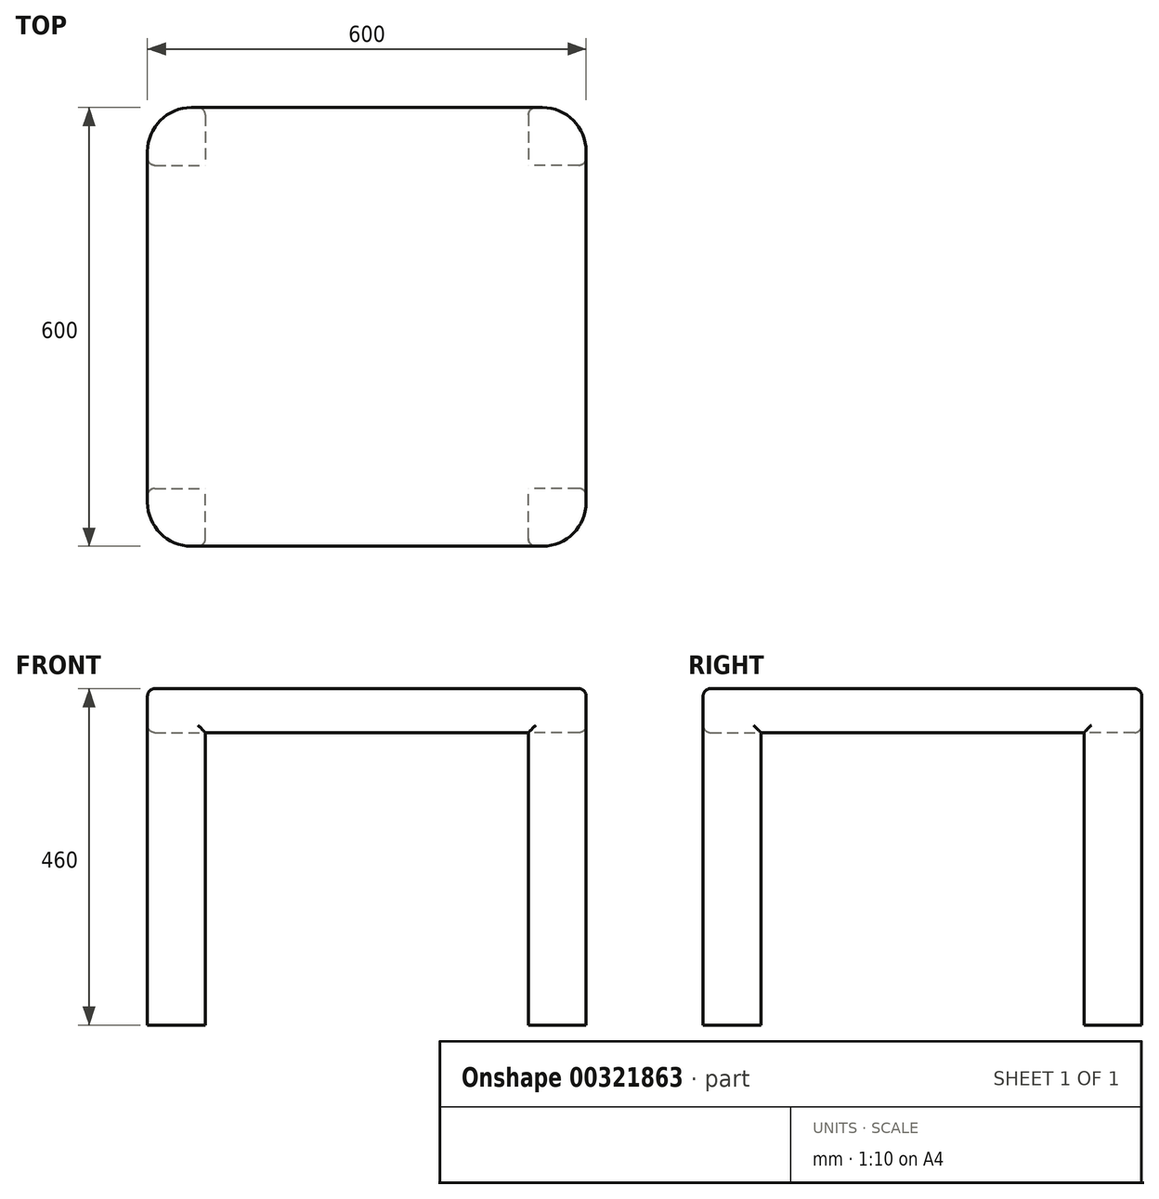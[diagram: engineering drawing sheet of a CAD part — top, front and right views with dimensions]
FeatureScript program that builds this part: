
annotation { "Feature Type Name" : "Feature", "Feature Type Description" : "" }
export const myFeature = defineFeature(function(context is Context, id is Id, definition is map)
    precondition{}
    {
        {
            var Q0;
            Q0=qCreatedBy(makeId("Top.planeOp"),FACE);
            var sketch = newSketch(context, id + "F0", { "sketchPlane" : qUnion([Q0])});
            skLineSegment(sketch, "E0.bottom", {"start": v(300, 300) * mm, "end": v(-300, 300) * mm});
            skLineSegment(sketch, "E0.top", {"start": v(300, -300) * mm, "end": v(-300, -300) * mm});
            skLineSegment(sketch, "E0.left", {"start": v(300, 300) * mm, "end": v(300, -300) * mm});
            skLineSegment(sketch, "E0.right", {"start": v(-300, 300) * mm, "end": v(-300, -300) * mm});
            skPoint(sketch, "E0.middle", {"position": v(0, 0) * mm});
            skSolve(sketch);
        }
        {
            var Q0;
            Q0=makeQuery(id+"F0.imprint","IMPRINT",FACE,{"disambiguationData":[TD([[makeQuery(id+"F0.imprint","IMPRINT",EDGE,{"derivedFrom":sQuery(id+"F0.wireOp",EDGE,"E0.bottom")}),1.0]])]});
            extrude(context, id + "F1", {"entities" : qUnion([Q0]), "depth" : 60 * mm});
        }
        {
            var Q0;
            Q0=makeQuery(id+"F1.opExtrude","CAP_FACE",FACE,{"disambiguationData":[OSD([sQuery(id+"F0.wireOp",EDGE,"E0.bottom"),sQuery(id+"F0.wireOp",EDGE,"E0.top"),sQuery(id+"F0.wireOp",EDGE,"E0.left"),sQuery(id+"F0.wireOp",EDGE,"E0.right")])],"isStart":true});
            var sketch = newSketch(context, id + "F2", { "sketchPlane" : qUnion([Q0])});
            skLineSegment(sketch, "E1", {"start": v(-300, 0) * mm, "end": v(300, 0) * mm});
            skLineSegment(sketch, "E2", {"start": v(0, -300) * mm, "end": v(0, 300) * mm});
            skLineSegment(sketch, "E3.bottom", {"start": v(-300, 300) * mm, "end": v(-220.95, 300) * mm});
            skLineSegment(sketch, "E3.top", {"start": v(-300, 220.95) * mm, "end": v(-220.95, 220.95) * mm});
            skLineSegment(sketch, "E3.left", {"start": v(-300, 300) * mm, "end": v(-300, 220.95) * mm});
            skLineSegment(sketch, "E3.right", {"start": v(-220.95, 300) * mm, "end": v(-220.95, 220.95) * mm});
            skLineSegment(sketch, "E4.MirrorCS", {"start": v(300, 220.95) * mm, "end": v(220.95, 220.95) * mm});
            skLineSegment(sketch, "E5.MirrorCS", {"start": v(300, 300) * mm, "end": v(300, 220.95) * mm});
            skLineSegment(sketch, "E6.MirrorCS", {"start": v(220.95, 300) * mm, "end": v(220.95, 220.95) * mm});
            skLineSegment(sketch, "E7.MirrorCS", {"start": v(300, 300) * mm, "end": v(220.95, 300) * mm});
            skLineSegment(sketch, "E8.MirrorCS", {"start": v(300, 0) * mm, "end": v(-300, 0) * mm});
            skLineSegment(sketch, "E9.MirrorCS", {"start": v(-220.95, -300) * mm, "end": v(-220.95, -220.95) * mm});
            skLineSegment(sketch, "E10.MirrorCS", {"start": v(-300, -300) * mm, "end": v(-220.95, -300) * mm});
            skLineSegment(sketch, "E11.MirrorCS", {"start": v(-300, -300) * mm, "end": v(-300, -220.95) * mm});
            skLineSegment(sketch, "E12.MirrorCS", {"start": v(-300, -220.95) * mm, "end": v(-220.95, -220.95) * mm});
            skLineSegment(sketch, "E13.MirrorCS", {"start": v(300, -300) * mm, "end": v(220.95, -300) * mm});
            skLineSegment(sketch, "E14.MirrorCS", {"start": v(220.95, -300) * mm, "end": v(220.95, -220.95) * mm});
            skLineSegment(sketch, "E15.MirrorCS", {"start": v(300, -220.95) * mm, "end": v(220.95, -220.95) * mm});
            skLineSegment(sketch, "E16.MirrorCS", {"start": v(300, -300) * mm, "end": v(300, -220.95) * mm});
            skSolve(sketch);
        }
        {
            var Q0;
            Q0 = qSketchRegion(id + "F2", true);
            extrude(context, id + "F3", {"entities" : qUnion([Q0]), "operationType" : NewBodyOperationType.ADD, "depth" : 400 * mm});
        }
        {
            var Q0;
            Q0=makeQuery(id+"F3.boolean.opBoolean","MERGE",EDGE,{"derivedFrom":[makeQuery(id+"F1.opExtrude","SWEPT_EDGE",EDGE,{"disambiguationData":[OSD([sQuery(id+"F0.wireOp",EDGE,"E0.top"),sQuery(id+"F0.wireOp",EDGE,"E0.right")])]}),makeQuery(id+"F3.opExtrude","SWEPT_EDGE",EDGE,{"disambiguationData":[OSD([sQuery(id+"F2.wireOp",EDGE,"E3.bottom"),sQuery(id+"F2.wireOp",EDGE,"E3.left")])]})]});
            var Q1;
            Q1=makeQuery(id+"F3.boolean.opBoolean","MERGE",EDGE,{"derivedFrom":[makeQuery(id+"F1.opExtrude","SWEPT_EDGE",EDGE,{"disambiguationData":[OSD([sQuery(id+"F0.wireOp",EDGE,"E0.bottom"),sQuery(id+"F0.wireOp",EDGE,"E0.right")])]}),makeQuery(id+"F3.opExtrude","SWEPT_EDGE",EDGE,{"disambiguationData":[OSD([sQuery(id+"F2.wireOp",EDGE,"E10.MirrorCS"),sQuery(id+"F2.wireOp",EDGE,"E11.MirrorCS")])]})]});
            var Q2;
            Q2=makeQuery(id+"F3.boolean.opBoolean","MERGE",EDGE,{"derivedFrom":[makeQuery(id+"F1.opExtrude","SWEPT_EDGE",EDGE,{"disambiguationData":[OSD([sQuery(id+"F0.wireOp",EDGE,"E0.bottom"),sQuery(id+"F0.wireOp",EDGE,"E0.left")])]}),makeQuery(id+"F3.opExtrude","SWEPT_EDGE",EDGE,{"disambiguationData":[OSD([sQuery(id+"F2.wireOp",EDGE,"E13.MirrorCS"),sQuery(id+"F2.wireOp",EDGE,"E16.MirrorCS")])]})]});
            var Q3;
            Q3=makeQuery(id+"F3.boolean.opBoolean","MERGE",EDGE,{"derivedFrom":[makeQuery(id+"F1.opExtrude","SWEPT_EDGE",EDGE,{"disambiguationData":[OSD([sQuery(id+"F0.wireOp",EDGE,"E0.top"),sQuery(id+"F0.wireOp",EDGE,"E0.left")])]}),makeQuery(id+"F3.opExtrude","SWEPT_EDGE",EDGE,{"disambiguationData":[OSD([sQuery(id+"F2.wireOp",EDGE,"E5.MirrorCS"),sQuery(id+"F2.wireOp",EDGE,"E7.MirrorCS")])]})]});
            fillet(context, id + "F4", {"entities" : qUnion([Q0, Q1, Q2, Q3]), "radius" : 60 * mm, "tangentPropagation" : true, "allowEdgeOverflow" : false});
        }
        {
            var Q0;
            Q0=makeQuery(id+"F1.opExtrude","CAP_EDGE",EDGE,{"disambiguationData":[OSD([sQuery(id+"F0.wireOp",EDGE,"E0.bottom")])],"isStart":false});
            var Q1;
            Q1=makeQuery(id+"F1.opExtrude","CAP_EDGE",EDGE,{"disambiguationData":[OSD([sQuery(id+"F0.wireOp",EDGE,"E0.bottom")])],"isStart":true});
            var Q2;
            Q2=makeQuery(id+"F3.opExtrude","SWEPT_EDGE",EDGE,{"disambiguationData":[OSD([sQuery(id+"F0.wireOp",EDGE,"E0.bottom"),sQuery(id+"F2.wireOp",EDGE,"E13.MirrorCS"),sQuery(id+"F2.wireOp",EDGE,"E14.MirrorCS")])]});
            var Q3;
            Q3=makeQuery(id+"F3.opExtrude","SWEPT_EDGE",EDGE,{"disambiguationData":[OSD([sQuery(id+"F0.wireOp",EDGE,"E0.bottom"),sQuery(id+"F2.wireOp",EDGE,"E9.MirrorCS"),sQuery(id+"F2.wireOp",EDGE,"E10.MirrorCS")])]});
            var Q4;
            Q4=makeQuery(id+"F1.opExtrude","CAP_EDGE",EDGE,{"disambiguationData":[OSD([sQuery(id+"F0.wireOp",EDGE,"E0.right")])],"isStart":true});
            var Q5;
            Q5=makeQuery(id+"F3.opExtrude","SWEPT_EDGE",EDGE,{"disambiguationData":[OSD([sQuery(id+"F0.wireOp",EDGE,"E0.right"),sQuery(id+"F2.wireOp",EDGE,"E11.MirrorCS"),sQuery(id+"F2.wireOp",EDGE,"E12.MirrorCS")])]});
            var Q6;
            Q6=makeQuery(id+"F3.opExtrude","SWEPT_EDGE",EDGE,{"disambiguationData":[OSD([sQuery(id+"F0.wireOp",EDGE,"E0.right"),sQuery(id+"F2.wireOp",EDGE,"E3.top"),sQuery(id+"F2.wireOp",EDGE,"E3.left")])]});
            var Q7;
            Q7=makeQuery(id+"F1.opExtrude","CAP_EDGE",EDGE,{"disambiguationData":[OSD([sQuery(id+"F0.wireOp",EDGE,"E0.top")])],"isStart":true});
            var Q8;
            Q8=makeQuery(id+"F3.opExtrude","SWEPT_EDGE",EDGE,{"disambiguationData":[OSD([sQuery(id+"F0.wireOp",EDGE,"E0.top"),sQuery(id+"F2.wireOp",EDGE,"E3.bottom"),sQuery(id+"F2.wireOp",EDGE,"E3.right")])]});
            var Q9;
            Q9=makeQuery(id+"F3.opExtrude","SWEPT_EDGE",EDGE,{"disambiguationData":[OSD([sQuery(id+"F0.wireOp",EDGE,"E0.top"),sQuery(id+"F2.wireOp",EDGE,"E6.MirrorCS"),sQuery(id+"F2.wireOp",EDGE,"E7.MirrorCS")])]});
            var Q10;
            Q10=makeQuery(id+"F1.opExtrude","CAP_EDGE",EDGE,{"disambiguationData":[OSD([sQuery(id+"F0.wireOp",EDGE,"E0.left")])],"isStart":true});
            var Q11;
            Q11=makeQuery(id+"F3.opExtrude","SWEPT_EDGE",EDGE,{"disambiguationData":[OSD([sQuery(id+"F0.wireOp",EDGE,"E0.left"),sQuery(id+"F2.wireOp",EDGE,"E4.MirrorCS"),sQuery(id+"F2.wireOp",EDGE,"E5.MirrorCS")])]});
            var Q12;
            Q12=makeQuery(id+"F3.opExtrude","SWEPT_EDGE",EDGE,{"disambiguationData":[OSD([sQuery(id+"F0.wireOp",EDGE,"E0.left"),sQuery(id+"F2.wireOp",EDGE,"E15.MirrorCS"),sQuery(id+"F2.wireOp",EDGE,"E16.MirrorCS")])]});
            fillet(context, id + "F5", {"entities" : qUnion([Q0, Q1, Q2, Q3, Q4, Q5, Q6, Q7, Q8, Q9, Q10, Q11, Q12]), "radius" : 10 * mm, "tangentPropagation" : true, "allowEdgeOverflow" : false});
        }
    });
